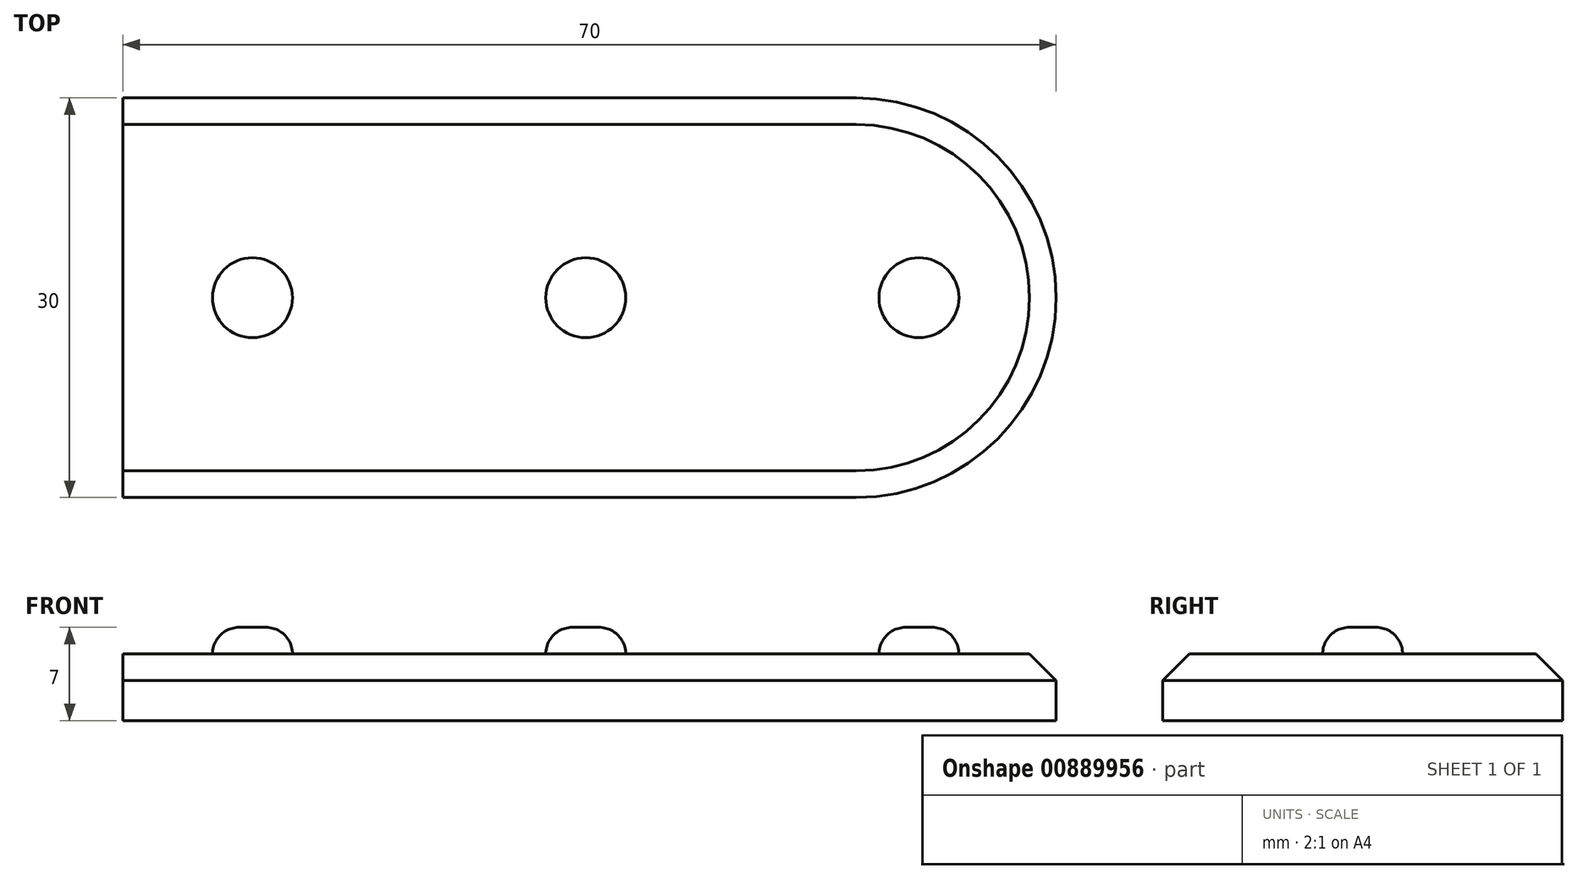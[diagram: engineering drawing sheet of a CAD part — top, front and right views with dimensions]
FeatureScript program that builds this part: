
annotation { "Feature Type Name" : "Feature", "Feature Type Description" : "" }
export const myFeature = defineFeature(function(context is Context, id is Id, definition is map)
    precondition{}
    {
        {
            var Q0;
            Q0=qCreatedBy(makeId("Top.planeOp"),FACE);
            var sketch = newSketch(context, id + "F0", { "sketchPlane" : qUnion([Q0])});
            skLineSegment(sketch, "E0.bottom", {"start": v(35, 15) * mm, "end": v(-35, 15) * mm});
            skLineSegment(sketch, "E0.top", {"start": v(35, -15) * mm, "end": v(-35, -15) * mm});
            skLineSegment(sketch, "E0.left", {"start": v(35, 15) * mm, "end": v(35, -15) * mm});
            skLineSegment(sketch, "E0.right", {"start": v(-35, 15) * mm, "end": v(-35, -15) * mm});
            skPoint(sketch, "E0.middle", {"position": v(0, 0) * mm});
            skSolve(sketch);
        }
        {
            var Q0;
            Q0=makeQuery(id+"F0.imprint","IMPRINT",FACE,{"disambiguationData":[TD([[makeQuery(id+"F0.imprint","IMPRINT",EDGE,{"derivedFrom":sQuery(id+"F0.wireOp",EDGE,"E0.bottom")}),1.0]])]});
            extrude(context, id + "F1", {"entities" : qUnion([Q0]), "depth" : 5 * mm, "offsetDistance" : 25 * mm});
        }
        {
            var Q0;
            Q0=makeQuery(id+"F1.opExtrude","SWEPT_EDGE",EDGE,{"disambiguationData":[OSD([sQuery(id+"F0.wireOp",EDGE,"E0.top"),sQuery(id+"F0.wireOp",EDGE,"E0.left")])]});
            var Q1;
            Q1=makeQuery(id+"F1.opExtrude","SWEPT_EDGE",EDGE,{"disambiguationData":[OSD([sQuery(id+"F0.wireOp",EDGE,"E0.bottom"),sQuery(id+"F0.wireOp",EDGE,"E0.left")])]});
            fillet(context, id + "F2", {"entities" : qUnion([Q0, Q1]), "radius" : 15 * mm, "tangentPropagation" : true, "allowEdgeOverflow" : false});
        }
        {
            var Q0;
            Q0=makeQuery(id+"F1.opExtrude","CAP_FACE",FACE,{"disambiguationData":[OSD([sQuery(id+"F0.wireOp",EDGE,"E0.bottom"),sQuery(id+"F0.wireOp",EDGE,"E0.top"),sQuery(id+"F0.wireOp",EDGE,"E0.left"),sQuery(id+"F0.wireOp",EDGE,"E0.right")])],"isStart":false});
            var sketch = newSketch(context, id + "F3", { "sketchPlane" : qUnion([Q0])});
            skCircle(sketch, "E1", {"center": v(-25.29, 0) * mm, "radius": 3 * mm});
            skLineSegment(sketch, "E2", {"start": v(-25.29, 0) * mm, "end": v(-0.29, 0) * mm});
            skCircle(sketch, "E3", {"center": v(-0.29, 0) * mm, "radius": 3 * mm});
            skLineSegment(sketch, "E4", {"start": v(-0.29, 0) * mm, "end": v(24.71, 0) * mm, "construction": true});
            skCircle(sketch, "E5", {"center": v(24.71, 0) * mm, "radius": 3 * mm});
            skSolve(sketch);
        }
        {
            var Q0;
            Q0=makeQuery(id+"F3.imprint","IMPRINT",FACE,{"disambiguationData":[TD([[makeQuery(id+"F3.imprint","IMPRINT",EDGE,{"derivedFrom":sQuery(id+"F3.wireOp",EDGE,"E1")}),1.0]])]});
            var Q1;
            Q1=makeQuery(id+"F3.imprint","IMPRINT",FACE,{"disambiguationData":[TD([[makeQuery(id+"F3.imprint","IMPRINT",EDGE,{"derivedFrom":sQuery(id+"F3.wireOp",EDGE,"E3")}),1.0]])]});
            var Q2;
            Q2=makeQuery(id+"F3.imprint","IMPRINT",FACE,{"disambiguationData":[TD([[makeQuery(id+"F3.imprint","IMPRINT",EDGE,{"derivedFrom":sQuery(id+"F3.wireOp",EDGE,"E5")}),1.0]])]});
            extrude(context, id + "F4", {"entities" : qUnion([Q0, Q1, Q2]), "operationType" : NewBodyOperationType.ADD, "depth" : 2 * mm, "offsetDistance" : 25 * mm});
        }
        {
            var Q0;
            Q0=makeQuery(id+"F4.opExtrude","CAP_EDGE",EDGE,{"disambiguationData":[OSD([sQuery(id+"F3.wireOp",EDGE,"E1")])],"isStart":false});
            var Q1;
            Q1=makeQuery(id+"F4.opExtrude","CAP_FACE",FACE,{"disambiguationData":[OSD([sQuery(id+"F3.wireOp",EDGE,"E3")])],"isStart":false});
            var Q2;
            Q2=makeQuery(id+"F4.opExtrude","CAP_EDGE",EDGE,{"disambiguationData":[OSD([sQuery(id+"F3.wireOp",EDGE,"E5")])],"isStart":false});
            fillet(context, id + "F5", {"entities" : qUnion([Q0, Q1, Q2]), "radius" : 2 * mm, "tangentPropagation" : true, "allowEdgeOverflow" : false});
        }
        {
            var Q0;
            Q0=makeQuery(id+"F1.opExtrude","CAP_EDGE",EDGE,{"disambiguationData":[OSD([sQuery(id+"F0.wireOp",EDGE,"E0.top")])],"isStart":false});
            chamfer(context, id + "F6", {"entities" : qUnion([Q0]), "width" : 2 * mm, "tangentPropagation" : true});
        }
    });
